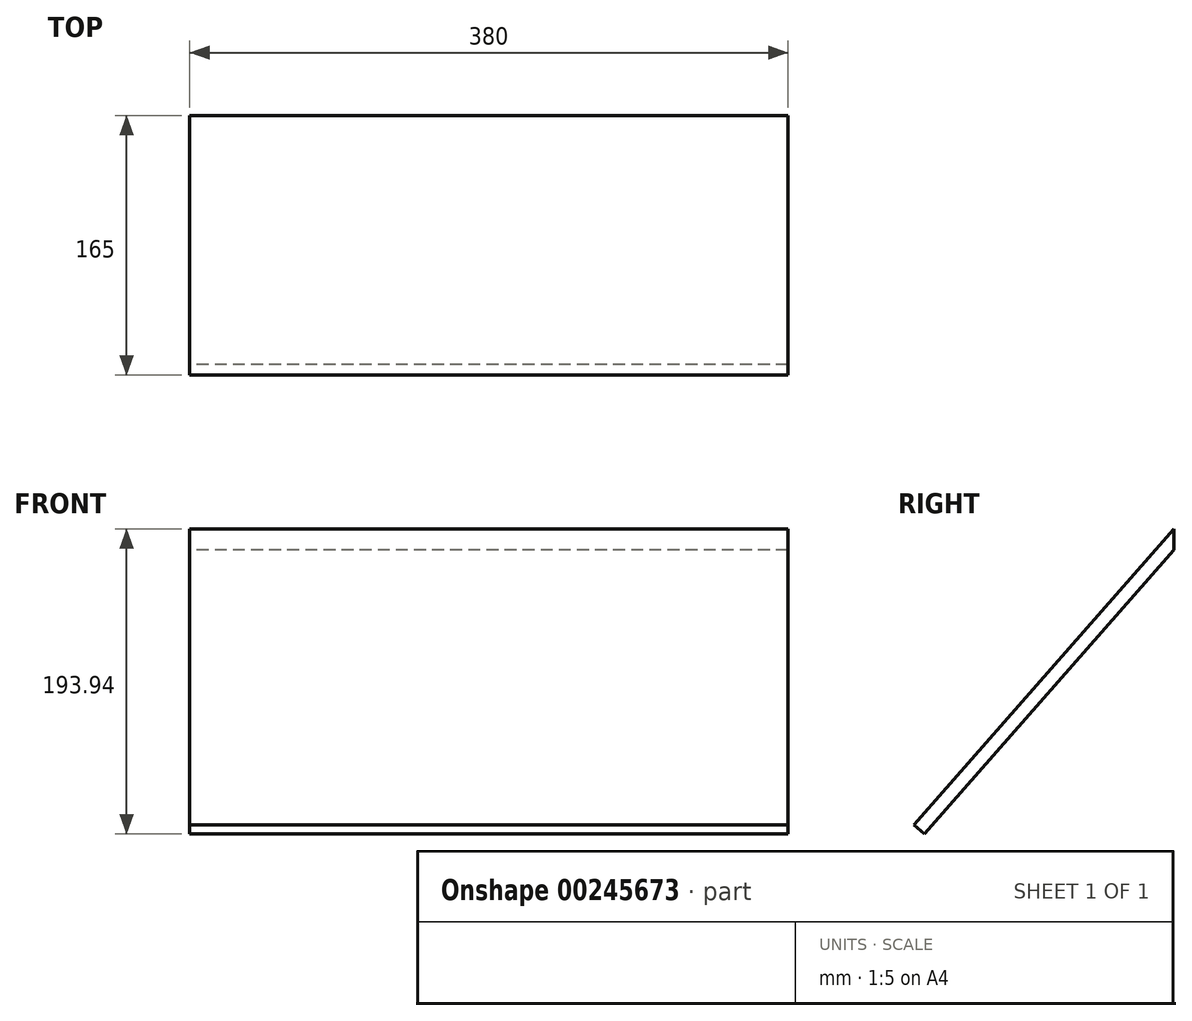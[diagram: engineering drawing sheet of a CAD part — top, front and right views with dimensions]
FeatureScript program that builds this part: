
annotation { "Feature Type Name" : "Feature", "Feature Type Description" : "" }
export const myFeature = defineFeature(function(context is Context, id is Id, definition is map)
    precondition{}
    {
        {
            var Q0;
            Q0=qCreatedBy(makeId("Right.planeOp"),FACE);
            var sketch = newSketch(context, id + "F0", { "sketchPlane" : qUnion([Q0])});
            skLineSegment(sketch, "E0", {"start": v(-112.91, -42.11) * mm, "end": v(52.09, 145.89) * mm});
            skLineSegment(sketch, "E1", {"start": v(-112.91, -42.11) * mm, "end": v(104.52, -42.11) * mm, "construction": true});
            skLineSegment(sketch, "E2", {"start": v(52.09, 145.89) * mm, "end": v(58.85, 139.95) * mm, "construction": true});
            skLineSegment(sketch, "E3", {"start": v(-112.91, -42.11) * mm, "end": v(-106.15, -48.05) * mm});
            skLineSegment(sketch, "E4", {"start": v(52.09, 145.89) * mm, "end": v(52.09, 127.46) * mm, "construction": true});
            skLineSegment(sketch, "E5", {"start": v(-106.15, -48.05) * mm, "end": v(52.09, 132.24) * mm});
            skLineSegment(sketch, "E6", {"start": v(52.09, 145.89) * mm, "end": v(52.09, 132.24) * mm});
            skSolve(sketch);
        }
        {
            var Q0;
            Q0 = qSketchRegion(id + "F0", true);
            extrude(context, id + "F1", {"entities" : qUnion([Q0]), "depth" : 380 * mm});
        }
    });
